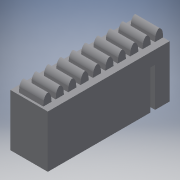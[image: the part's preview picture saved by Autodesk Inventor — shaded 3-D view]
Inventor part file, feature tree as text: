
AUTODESK INVENTOR PART (.ipt)
format: ipt  version: 2016 (Build 200138000, 138)  size: 381,440 bytes
history: native  units: in
note: dims shown in document units (in); Inventor stores cm internally (conversion verified against a paired STEP export)
features: extrude x9, sketch x9, projected_geometry x4
ambient origin geometry x8: Origin, YZ Plane, XZ Plane, XY Plane, X Axis, Y Axis, Z Axis, Center Point
bodies: Body1 (feature_tree)
feature tree (22):
  extrude  "Extrusion2"  Depth=0.435in
  sketch  "Sketch3"  dims[d6=0.385in d7=0.0in d9=0.092in]
  extrude  "Extrusion4"  Depth=0.385in
  extrude  "Extrusion6"  Depth=0.075in
  extrude  "Extrusion7"  Depth=0.05in
  extrude  "Extrusion8"  Depth=0.1in TaperAngle=0.0deg
  extrude  "Extrusion9"  Depth=0.385in TaperAngle=0.0deg
  extrude  "Extrusion10"  Depth=0.5814in
  extrude  "Extrusion11"  Depth=0.25in TaperAngle=0.0deg
  extrude  "Extrusion12"  Depth=0.385in TaperAngle=0.0deg
  sketch  "Sketch2"  dims[d4=2.5in d5=0.435in]
  sketch  "Sketch4"  dims[d28=0.075in d29=0.075in]
  sketch  "Sketch5"  dims[d31=0.1in d32=0.05in]
  projected_geometry  "Projected Loop1"
  projected_geometry  "Projected Loop2"
  projected_geometry  "Projected Loop3"
  sketch  "Sketch6"  dims[d33=0.4in d34=0.0in d58=0.1in d59=0.0in]
  sketch  "Sketch7"  dims[d60=0.1in d61=0.385in d62=0.0in]
  sketch  "Sketch8"  dims[d63=0.5814in d64=0.5814in]
  sketch  "Sketch9"  dims[d72=7.874in d74=0.1271in d75=0.3937in d77=1.0in d79=0.25in d80=0.0in]
  projected_geometry  "Projected Loop4"
  sketch  "Sketch10"  dims[d81=0.05in d82=0.385in d83=0.0in d84=0.15in d85=0.05in d86=0.4in d87=0.385in d88=0.0in d89=0.385in d90=0.0in d91=1.0in d92=0.0in]
